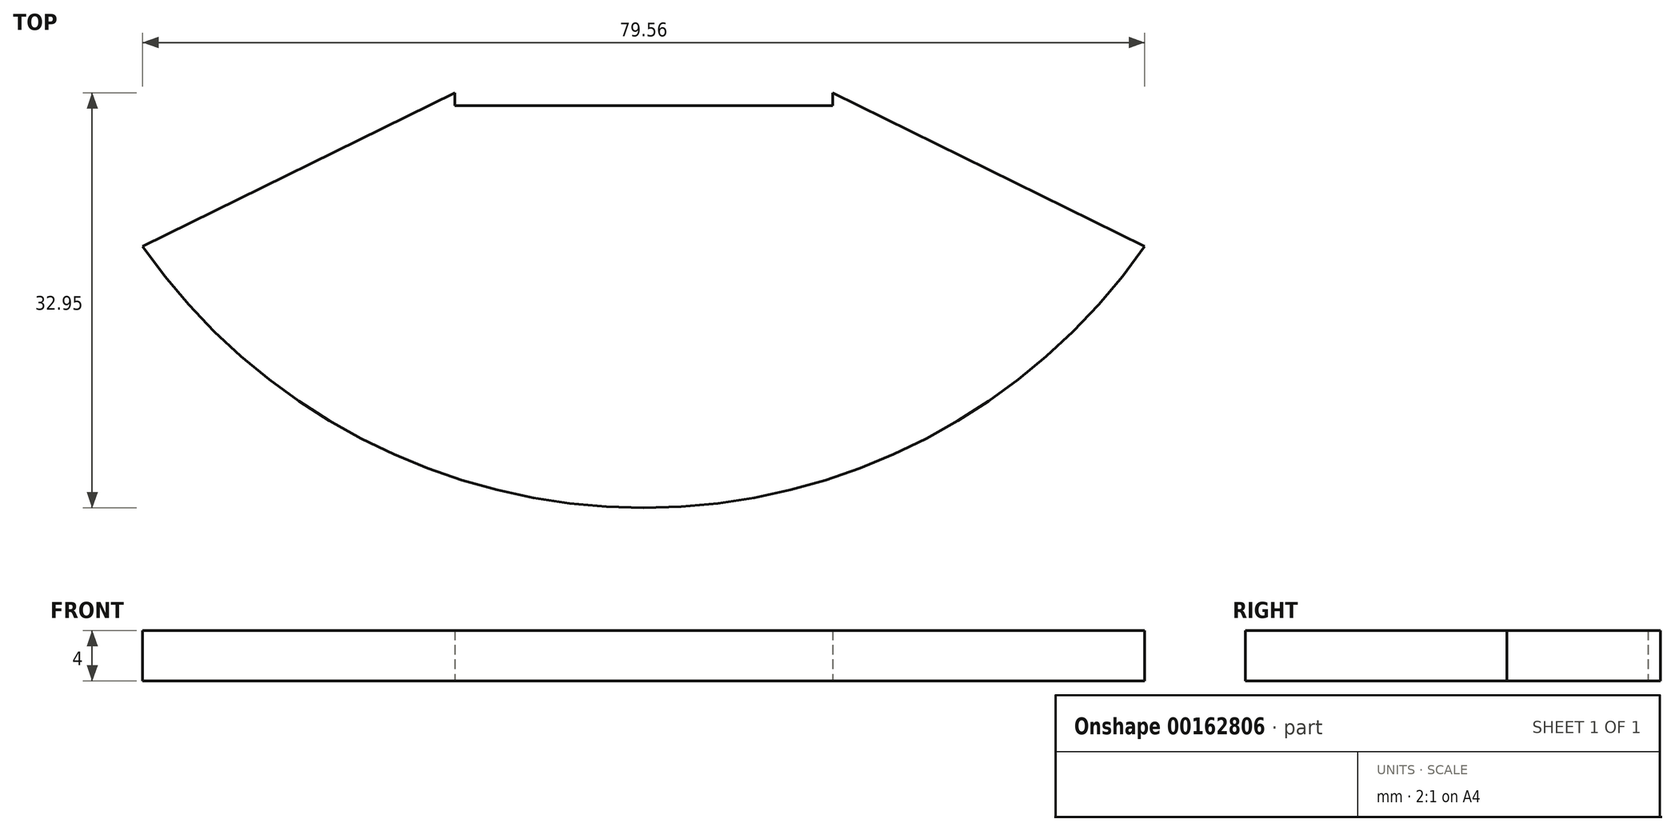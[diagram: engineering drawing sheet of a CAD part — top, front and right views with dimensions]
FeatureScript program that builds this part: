
annotation { "Feature Type Name" : "Feature", "Feature Type Description" : "" }
export const myFeature = defineFeature(function(context is Context, id is Id, definition is map)
    precondition{}
    {
        {
            var Q0;
            Q0=qCreatedBy(makeId("Top.planeOp"),FACE);
            var sketch = newSketch(context, id + "F0", { "sketchPlane" : qUnion([Q0])});
            skCircle(sketch, "E0", {"center": v(0, 0) * mm, "radius": 48.5 * mm});
            skLineSegment(sketch, "E1.bottom", {"start": v(15, 16.55) * mm, "end": v(-15, 16.55) * mm});
            skLineSegment(sketch, "E1.top", {"start": v(15, -16.55) * mm, "end": v(-15, -16.55) * mm});
            skLineSegment(sketch, "E1.left", {"start": v(15, 16.55) * mm, "end": v(15, -16.55) * mm});
            skLineSegment(sketch, "E1.right", {"start": v(-15, 16.55) * mm, "end": v(-15, -16.55) * mm});
            skLineSegment(sketch, "E2", {"start": v(-15, -15.55) * mm, "end": v(-39.78, -27.74) * mm});
            skLineSegment(sketch, "E3", {"start": v(0, 0) * mm, "end": v(0, -16.55) * mm, "construction": true});
            skLineSegment(sketch, "E4.MirrorCS", {"start": v(15, -15.55) * mm, "end": v(39.78, -27.74) * mm});
            skSolve(sketch);
        }
        {
            var Q0;
            {var subQ1=sQuery(id+"F0.wireOp",EDGE,"E1.top");Q0=makeQuery(id+"F0.imprint","IMPRINT",FACE,{"disambiguationData":[TD([[makeQuery(id+"F0.imprint","IMPRINT",EDGE,{"derivedFrom":subQ1}),1.0]])]});}
            extrude(context, id + "F1", {"entities" : qUnion([Q0]), "depth" : 4 * mm});
        }
    });
